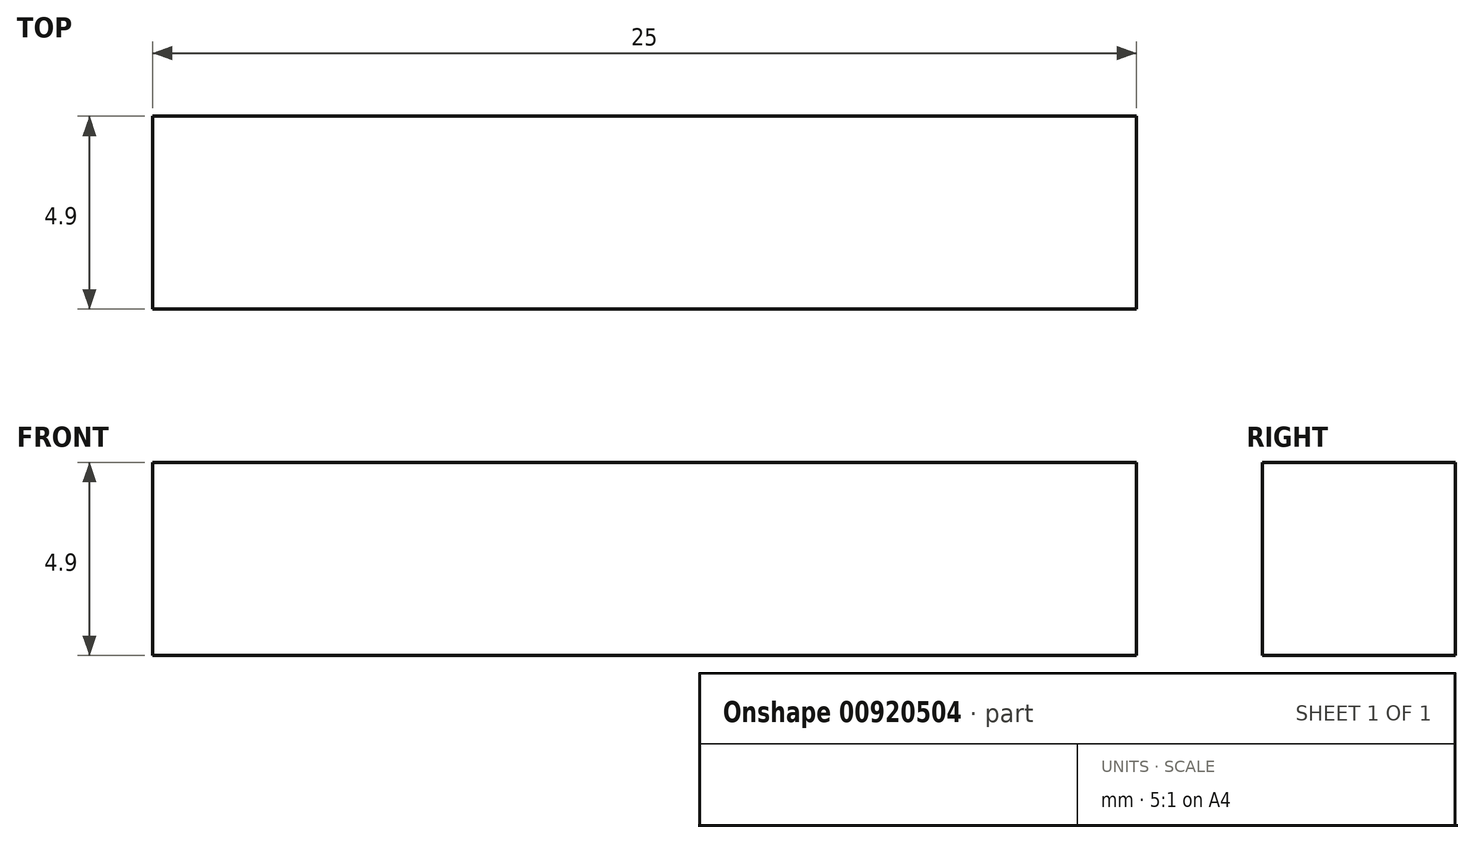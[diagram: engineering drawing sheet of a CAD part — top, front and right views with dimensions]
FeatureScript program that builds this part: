
annotation { "Feature Type Name" : "Feature", "Feature Type Description" : "" }
export const myFeature = defineFeature(function(context is Context, id is Id, definition is map)
    precondition{}
    {
        {
            var Q0;
            Q0=qCreatedBy(makeId("Top.planeOp"),FACE);
            var sketch = newSketch(context, id + "F0", { "sketchPlane" : qUnion([Q0])});
            skLineSegment(sketch, "E0.bottom", {"start": v(-20.82, 9.7) * mm, "end": v(4.18, 9.7) * mm});
            skLineSegment(sketch, "E0.top", {"start": v(-20.82, 4.8) * mm, "end": v(4.18, 4.8) * mm});
            skLineSegment(sketch, "E0.left", {"start": v(-20.82, 9.7) * mm, "end": v(-20.82, 4.8) * mm});
            skLineSegment(sketch, "E0.right", {"start": v(4.18, 9.7) * mm, "end": v(4.18, 4.8) * mm});
            skSolve(sketch);
        }
        {
            var Q0;
            Q0=makeQuery(id+"F0.imprint","IMPRINT",FACE,{"disambiguationData":[TD([[makeQuery(id+"F0.imprint","IMPRINT",EDGE,{"derivedFrom":sQuery(id+"F0.wireOp",EDGE,"E0.bottom")}),-1.0]])]});
            extrude(context, id + "F1", {"entities" : qUnion([Q0]), "depth" : 4.9 * mm, "offsetDistance" : 25 * mm});
        }
    });
